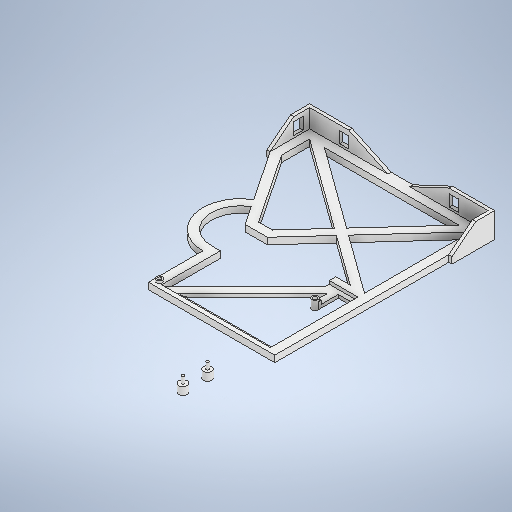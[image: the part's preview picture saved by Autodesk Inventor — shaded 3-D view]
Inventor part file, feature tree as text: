
AUTODESK INVENTOR PART (.ipt)
format: ipt  version: 2025.2 (Build 292293000, 293)  size: 449,536 bytes
history: native  units: mm
features: extrude x8, sketch x6
ambient origin geometry x8: Origin, YZ Plane, XZ Plane, XY Plane, X Axis, Y Axis, Z Axis, Center Point
bodies: Solid1 (feature_tree)
feature tree (14):
  sketch  "Sketch1"  dims[d0=52.786mm d1=82.0mm]
  extrude  "Extrusion1"  Depth=82.0mm
  extrude  "Extrusion2"  Depth=5.0mm
  extrude  "Extrusion3"  Depth=58.0mm
  extrude  "Extrusion4"  Depth=25.0mm
  extrude  "Extrusion5"  Depth=10.23mm
  extrude  "Extrusion6"  Depth=17.153mm
  extrude  "Extrusion7"  Depth=3.0mm
  extrude  "Extrusion8"  Depth=25.0mm
  sketch  "Sketch4"  dims[d2=18.104mm d3=5.0mm]
  sketch  "Sketch5"  dims[d4=40.214mm d5=58.0mm]
  sketch  "Sketch6"  dims[d6=25.0mm d7=25.52195mm]
  sketch  "Sketch7"  dims[d8=41.72mm d9=10.23mm]
  sketch  "Sketch8"  dims[d12=4.0mm d13=17.153mm d14=27.568mm d15=25.0mm d16=13.153mm d17=4.0mm d18=0.0mm d19=4.0mm d20=6.808mm d21=83.035mm d22=13.14mm d23=5.0mm d24=4.0mm d25=9.214mm d26=3.19mm d27=2.9mm d28=1.8mm d29=3.0mm d30=2.0mm d31=2.9mm d32=1.8mm d33=4.0mm d34=3.0mm d35=0.0mm d36=4.0mm d37=0.0mm d38=2.0mm d39=0.0mm d40=2.0mm d41=7.75mm d42=1.5mm d43=0.0mm d44=8.5mm d45=17.94mm d46=20.0mm d47=2.3mm d48=2.3mm d49=5.2mm d50=4.2mm d51=1.5mm d52=0.0mm d53=19.604mm d55=13.826mm d56=1.5mm d57=0.0mm d58=13.826mm d59=4.5mm d60=5.5mm d61=2.0mm d62=4.5mm d63=1.5mm d64=0.0mm d65=3.5mm d66=0.0mm d67=1.3mm d68=1.35mm d69=3.0mm d70=0.0mm]
